# Revit family: 2070016
name_source: partatom
category: Lighting Fixtures
revit_build: Autodesk Revit 2018 (Build: 20170223_1515(x64)
units: mm (PartAtom-declared; Revit-internal decimal feet)

## family parameters
Cut with Voids When Loaded = No
Host = Face
Light Source = Yes
OmniClass Number = 23.80.70.11.17
OmniClass Title = Specialized Lighting by Location or Use
Part Type = Normal
Room Calculation Point = No
Round Connector Dimension = Use Diameter
Shared = No

## types (1)
- 2070016 EXPOSPOT 70 FIX RA90 3000K MB WHITE
    Apparent Load = 21 VA
    Assembly Code = D5020200
    Average Life = 50 000h
    Beam Angle = 43°
    Body Material = Aluminum_Sylvania_Expospot_White
    CRI = 80Ra
    Color Filter = 16777215
    Colour Variation Initial = 3SDCM
    Control Gear Mounting = Remote
    Control Gear Required = No
    Control Gear Type = Electronic
    Cooling Big Axis = 43 mm  [stored 0.141076 ft]
    Cooling Material = Plastic_Sylvania_Expospot_Black
    Cooling Small Axis = 32 mm  [stored 0.104987 ft]
    Cutout Diameter = 100 mm  [stored 0.328084 ft]
    Default Elevation = 0 mm  [stored 0 ft]
    Description = Specifically designed for Retail and Display applications. I.e. Supermarkets, Fashion Retail, Department stores. Build around a 70mm reflector and lens combination.
    Diameter = 110 mm  [stored 0.360892 ft]
    Diffuser Material = Acrylic_Sylvania_Expospot_3000K
    Dimmable = N
    Dimming Lamp Color Temperature Shift = <None>
    Drive Current = 500mA
    Electrical Protection = Class II
    Emit Shape Visible in Rendering = No
    Emit from Circle Diameter = 86 mm  [stored 0.282152 ft]
    Glow Wire Test = 850 °C
    Height = 101 mm  [stored 0.331365 ft]
    IK Rating = IK02
    IP Rating = IP20
    Inrush Current = 28 A
    Inrush Duration = 139µs
    LOR = 100%
    Lamp = LED
    Lamp Power Factor = 0.9
    Manufacturer = Feilo Sylvania
    Max. Luminaires per 10A B Breaker = 19
    Max. Luminaires per 10A C Breaker = 31
    Max. Luminaires per 13A B Breaker = 25
    Max. Luminaires per 13A C Breaker = 41
    Max. Luminaires per 16A B Breaker = 31
    Max. Luminaires per 16A C Breaker = 51
    Max. Luminaires per 20A B Breaker = 42
    Max. Luminaires per 20A C Breaker = 70
    Model = EXPOSPOT 70 FIXED RA90 3000K MB WHITE
    Nominal Frequency = 50/60Hz
    Photobiological Risk Group = RG1
    Photometric Web File = 2070016.ies
    Product Code = 0060226
    Product Family = EXPOSPOT 70 FIXED
    Product Page URL = http://www.sylvania-lighting.com
    Radius = 55 mm  [stored 0.180446 ft]
    Reflector Material = Aluminum_Sylvania_Expospot_Polished
    Tilt Angle = -90°
    Total Power Consumption = 21 W
    URL = 0.9
    Voltage = 240 V
    Voltage Comments = 220-240V~
    Weight = 1 kg

note: [stored X ft] marks values corroborated as IEEE doubles in the binary element streams (Revit-internal decimal feet)

## geometry (parser evidence)
native form markers: Sweep x2
no freeform markers — native parametric forms only
